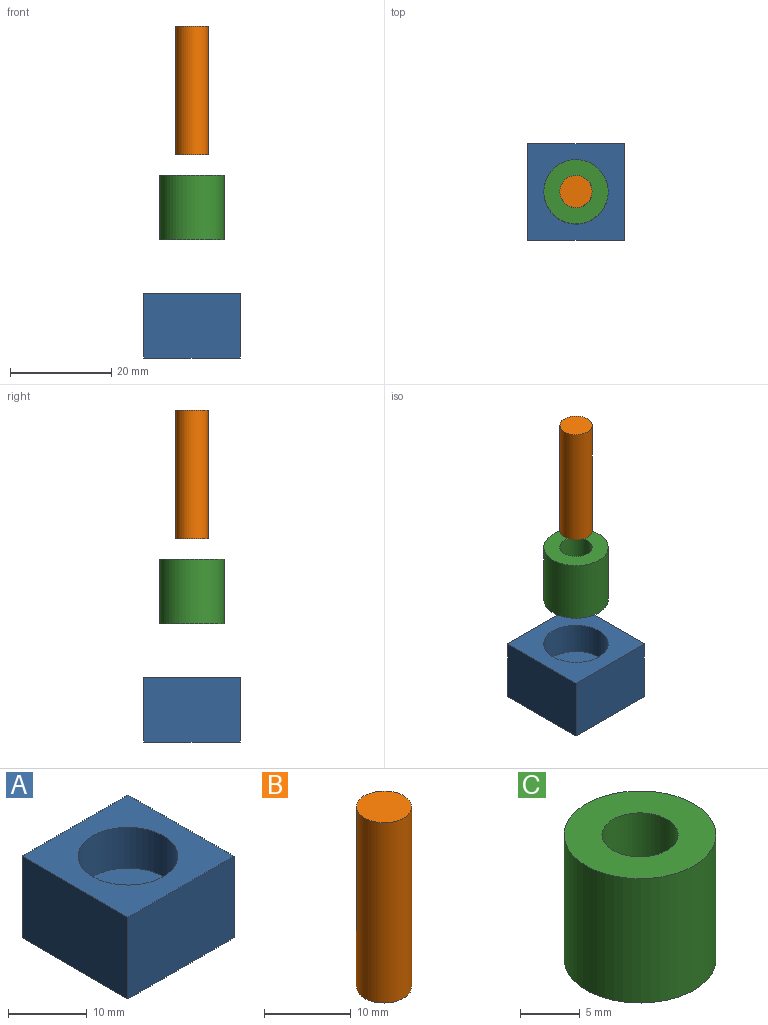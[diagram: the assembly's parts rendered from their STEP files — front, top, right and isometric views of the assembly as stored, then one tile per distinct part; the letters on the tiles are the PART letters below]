
ASSEMBLY  parts=3 mates=2
PART A: 8 faces, bbox 19.1x19.1x12.7 mm
  f0: plane 19.05x12.7mm, normal (1,0,0), area 241.9mm2, adj f1,f3,f4,f5
  f1: plane 19.05x12.7mm, normal (0,1,0), area 241.9mm2, adj f0,f2,f4,f5
  f2: plane 19.05x12.7mm, normal (-1,0,0), area 241.9mm2, adj f1,f3,f4,f5
  f3: plane 19.05x12.7mm, normal (0,-1,0), area 241.9mm2, adj f0,f2,f4,f5
  f4: plane 19.05x19.05mm, normal (0,0,1), area 236.2mm2, adj f0,f1,f2,f3,f6
  f5: plane 19.05x19.05mm, normal (0,0,-1), area 362.9mm2, adj f0,f1,f2,f3
  f6: cylinder r=6.35mm len=12.7mm, axis (0,0,1), area 253.4mm2, adj f4,f7
  f7: plane 12.7x12.7mm, normal (0,0,1), area 126.7mm2, adj f6
PART B: 3 faces, bbox 6.3x6.3x25.4 mm
  f0: cylinder r=3.17mm len=25.4mm, axis (0,0,-1), area 505.7mm2, adj f1,f2
  f1: plane 6.34x6.34mm, normal (0,0,1), area 31.5mm2, adj f0
  f2: plane 6.34x6.34mm, normal (0,0,-1), area 31.5mm2, adj f0
PART C: 4 faces, bbox 12.7x12.7x12.7 mm
  f0: cylinder r=3.17mm len=12.7mm, axis (0,0,-1), area 253.4mm2, adj f2,f3
  f1: cylinder r=6.34mm len=12.7mm, axis (0,0,-1), area 506.1mm2, adj f2,f3
  f2: plane 12.68x12.68mm, normal (0,0,1), area 94.7mm2, adj f0,f1
  f3: plane 12.68x12.68mm, normal (0,0,-1), area 94.7mm2, adj f0,f1
PLACE A at identity fixed
PLACE B t=(0,0,40.05)mm
PLACE C t=(0,0,23.35)mm
MATE fastened A.f6 <-> C.f0  axis (0,0,1) through (0,0,6.35)mm
MATE fastened B.f0 <-> C.f1  axis (0,0,-1) through (0,0,40.05)mm
